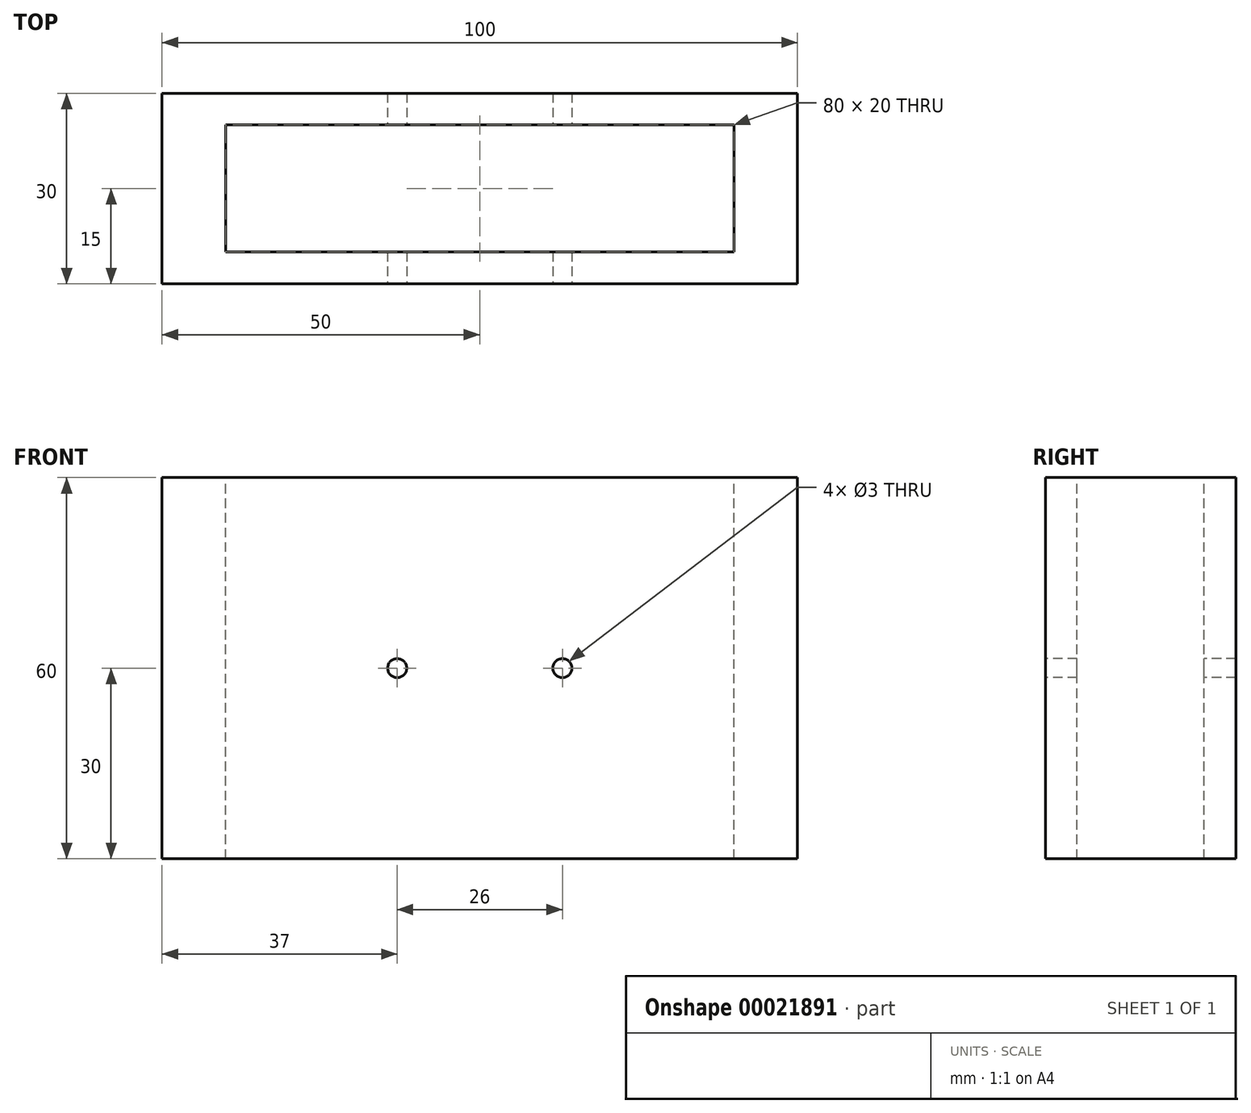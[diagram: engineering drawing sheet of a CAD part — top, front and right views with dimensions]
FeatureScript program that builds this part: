
annotation { "Feature Type Name" : "Feature", "Feature Type Description" : "" }
export const myFeature = defineFeature(function(context is Context, id is Id, definition is map)
    precondition{}
    {
        {
            var Q0;
            Q0=qCreatedBy(makeId("Front.planeOp"),FACE);
            var sketch = newSketch(context, id + "F0", { "sketchPlane" : qUnion([Q0])});
            skLineSegment(sketch, "E0.rect.bottom", {"start": v(-50, 30) * mm, "end": v(50, 30) * mm});
            skLineSegment(sketch, "E0.rect.top", {"start": v(-50, -30) * mm, "end": v(50, -30) * mm});
            skLineSegment(sketch, "E0.rect.left", {"start": v(-50, 30) * mm, "end": v(-50, -30) * mm});
            skLineSegment(sketch, "E0.rect.right", {"start": v(50, 30) * mm, "end": v(50, -30) * mm});
            skPoint(sketch, "E0.rect.middle", {"position": v(0, 0) * mm});
            skSolve(sketch);
        }
        {
            var Q0;
            Q0=makeQuery(id+"F0.imprint","IMPRINT",FACE,{"disambiguationData":[TD([[makeQuery(id+"F0.imprint","IMPRINT",EDGE,{"derivedFrom":sQuery(id+"F0.wireOp",EDGE,"E0.rect.bottom")}),-1.0]])]});
            extrude(context, id + "F1", {"entities" : qUnion([Q0]), "depth" : 30 * mm});
        }
        {
            var Q0;
            Q0=makeQuery(id+"F1.opExtrude","SWEPT_FACE",FACE,{"disambiguationData":[OSD([sQuery(id+"F0.wireOp",EDGE,"E0.rect.bottom")])]});
            var sketch = newSketch(context, id + "F2", { "sketchPlane" : qUnion([Q0])});
            skLineSegment(sketch, "E1.rect.bottom", {"start": v(-40, -5) * mm, "end": v(40, -5) * mm});
            skLineSegment(sketch, "E1.rect.top", {"start": v(-40, -25) * mm, "end": v(40, -25) * mm});
            skLineSegment(sketch, "E1.rect.left", {"start": v(-40, -5) * mm, "end": v(-40, -25) * mm});
            skLineSegment(sketch, "E1.rect.right", {"start": v(40, -5) * mm, "end": v(40, -25) * mm});
            skPoint(sketch, "E1.rect.middle", {"position": v(0, -15) * mm});
            skSolve(sketch);
        }
        {
            var Q0;
            Q0=makeQuery(id+"F2.imprint","IMPRINT",FACE,{"disambiguationData":[TD([[makeQuery(id+"F2.imprint","IMPRINT",EDGE,{"derivedFrom":sQuery(id+"F2.wireOp",EDGE,"E1.rect.bottom")}),-1.0]])]});
            extrude(context, id + "F3", {"entities" : qUnion([Q0]), "operationType" : NewBodyOperationType.REMOVE, "oppositeDirection" : true, "depth" : 60 * mm});
        }
        {
            var Q0;
            Q0=makeQuery(id+"F1.opExtrude","CAP_FACE",FACE,{"disambiguationData":[OSD([sQuery(id+"F0.wireOp",EDGE,"E0.rect.bottom"),sQuery(id+"F0.wireOp",EDGE,"E0.rect.top"),sQuery(id+"F0.wireOp",EDGE,"E0.rect.left"),sQuery(id+"F0.wireOp",EDGE,"E0.rect.right")])],"isStart":false});
            var sketch = newSketch(context, id + "F4", { "sketchPlane" : qUnion([Q0])});
            skLineSegment(sketch, "E2", {"start": v(-13, 0) * mm, "end": v(13, 0) * mm});
            skCircle(sketch, "E3", {"center": v(-13, 0) * mm, "radius": 1.5 * mm});
            skCircle(sketch, "E4", {"center": v(13, 0) * mm, "radius": 1.5 * mm});
            skSolve(sketch);
        }
        {
            var Q0;
            Q0=makeQuery(id+"F4.imprint","IMPRINT",FACE,{"disambiguationData":[TD([[makeQuery(id+"F4.imprint","IMPRINT",EDGE,{"derivedFrom":sQuery(id+"F4.wireOp",EDGE,"E3")}),1.0]])]});
            var Q1;
            Q1=makeQuery(id+"F4.imprint","IMPRINT",FACE,{"disambiguationData":[TD([[makeQuery(id+"F4.imprint","IMPRINT",EDGE,{"derivedFrom":sQuery(id+"F4.wireOp",EDGE,"E4")}),1.0]])]});
            extrude(context, id + "F5", {"entities" : qUnion([Q0, Q1]), "operationType" : NewBodyOperationType.REMOVE, "oppositeDirection" : true, "depth" : 30 * mm});
        }
    });
